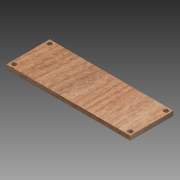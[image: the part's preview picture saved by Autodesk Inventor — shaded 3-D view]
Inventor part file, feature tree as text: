
AUTODESK INVENTOR PART (.ipt)
format: ipt  version: 2012 (Build 160160000, 160)  size: 99,328 bytes
history: native  units: mm
features: extrude x1, sketch x1
ambient origin geometry x8: Origin, YZ Plane, XZ Plane, XY Plane, X Axis, Y Axis, Z Axis, Center Point
bodies: Solid1 (feature_tree)
feature tree (2):
  extrude  "Extrusion1"  Depth=75.0mm
  sketch  "Sketch1"  dims[d0=215.0mm d1=75.0mm d2=8.0mm d3=6.5mm d4=6.5mm d5=6.5mm d6=6.5mm d7=6.5mm d8=6.5mm d9=6.5mm d10=6.5mm d11=7.5mm d12=0.0mm]
